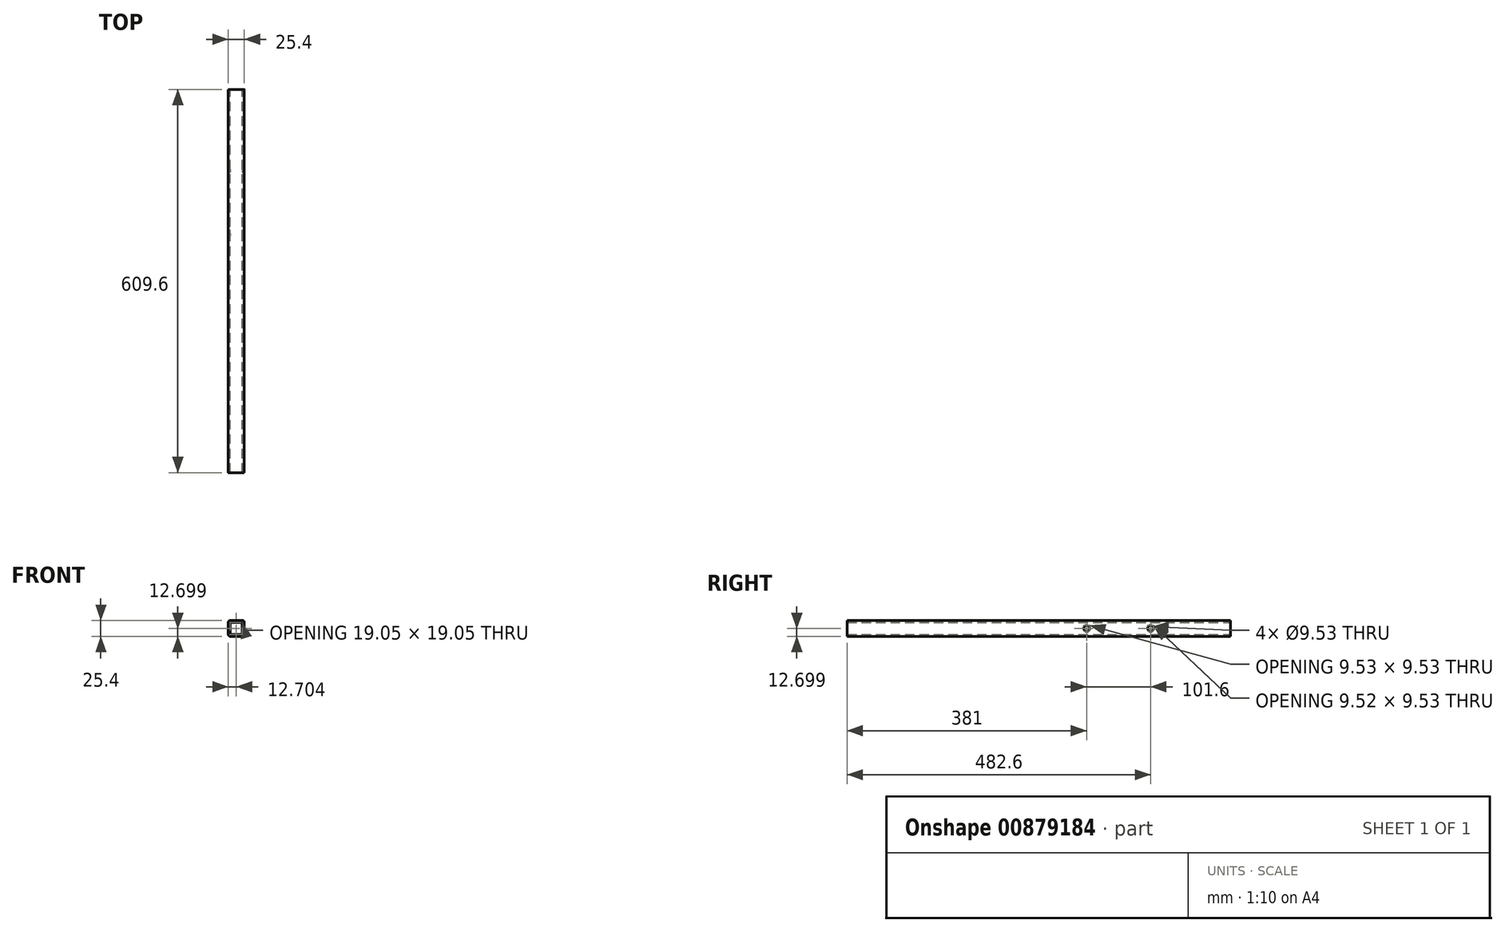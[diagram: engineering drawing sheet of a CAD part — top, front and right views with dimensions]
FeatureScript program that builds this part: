
annotation { "Feature Type Name" : "Feature", "Feature Type Description" : "" }
export const myFeature = defineFeature(function(context is Context, id is Id, definition is map)
    precondition{}
    {
        {
            var Q0;
            Q0=qCreatedBy(makeId("Front.planeOp"),FACE);
            var sketch = newSketch(context, id + "F0", { "sketchPlane" : qUnion([Q0])});
            skLineSegment(sketch, "E0.bottom", {"start": v(9.13, -11.87) * mm, "end": v(-9.92, -11.87) * mm});
            skLineSegment(sketch, "E0.top", {"start": v(9.13, 13.53) * mm, "end": v(-9.92, 13.53) * mm});
            skLineSegment(sketch, "E0.left", {"start": v(12.3, -8.7) * mm, "end": v(12.3, 10.35) * mm});
            skLineSegment(sketch, "E0.right", {"start": v(-13.1, -8.7) * mm, "end": v(-13.1, 10.35) * mm});
            skLineSegment(sketch, "E1.bottom", {"start": v(5.95, -8.7) * mm, "end": v(-6.75, -8.7) * mm});
            skLineSegment(sketch, "E1.top", {"start": v(5.95, 10.35) * mm, "end": v(-6.75, 10.35) * mm});
            skLineSegment(sketch, "E1.left", {"start": v(9.13, -5.52) * mm, "end": v(9.13, 7.18) * mm});
            skLineSegment(sketch, "E1.right", {"start": v(-9.92, -5.52) * mm, "end": v(-9.92, 7.18) * mm});
            skPoint(sketch, "E2.visualSharp", {"position": v(9.13, 10.35) * mm});
            skArc(sketch, "E2.filletArc", {"start": v(9.13, 7.18) * mm, "mid": v(8.2, 9.42) * mm, "end": v(5.95, 10.35) * mm});
            skPoint(sketch, "E3.visualSharp", {"position": v(-9.92, 10.35) * mm});
            skArc(sketch, "E3.filletArc", {"start": v(-6.75, 10.35) * mm, "mid": v(-9, 9.42) * mm, "end": v(-9.92, 7.18) * mm});
            skPoint(sketch, "E4.visualSharp", {"position": v(-9.92, -8.7) * mm});
            skArc(sketch, "E4.filletArc", {"start": v(-9.92, -5.52) * mm, "mid": v(-9, -7.77) * mm, "end": v(-6.75, -8.7) * mm});
            skPoint(sketch, "E5.visualSharp", {"position": v(9.13, -8.7) * mm});
            skArc(sketch, "E5.filletArc", {"start": v(5.95, -8.7) * mm, "mid": v(8.2, -7.77) * mm, "end": v(9.13, -5.52) * mm});
            skPoint(sketch, "E6.visualSharp", {"position": v(12.3, 13.53) * mm});
            skArc(sketch, "E6.filletArc", {"start": v(12.3, 10.35) * mm, "mid": v(11.37, 12.6) * mm, "end": v(9.13, 13.53) * mm});
            skPoint(sketch, "E7.visualSharp", {"position": v(-13.1, 13.53) * mm});
            skArc(sketch, "E7.filletArc", {"start": v(-9.92, 13.53) * mm, "mid": v(-12.17, 12.6) * mm, "end": v(-13.1, 10.35) * mm});
            skPoint(sketch, "E8.visualSharp", {"position": v(-13.1, -11.87) * mm});
            skArc(sketch, "E8.filletArc", {"start": v(-13.1, -8.7) * mm, "mid": v(-12.17, -10.94) * mm, "end": v(-9.92, -11.87) * mm});
            skPoint(sketch, "E9.visualSharp", {"position": v(12.3, -11.87) * mm});
            skArc(sketch, "E9.filletArc", {"start": v(9.13, -11.87) * mm, "mid": v(11.37, -10.94) * mm, "end": v(12.3, -8.7) * mm});
            skSolve(sketch);
        }
        {
            var Q0;
            Q0=qSketchRegion(id+"F0",true);
            extrude(context, id + "F1", {"entities" : qUnion([Q0]), "depth" : 609.6 * mm, "offsetDistance" : 25.4 * mm});
        }
        {
            var Q0;
            Q0=makeQuery(id+"F1.opExtrude","SWEPT_FACE",FACE,{"disambiguationData":[OSD([sQuery(id+"F0.wireOp",EDGE,"E0.left")])]});
            var sketch = newSketch(context, id + "F2", { "sketchPlane" : qUnion([Q0])});
            skCircle(sketch, "E10", {"center": v(-228.6, 0.83) * mm, "radius": 4.76 * mm});
            skCircle(sketch, "E11", {"center": v(-127, 0.83) * mm, "radius": 4.76 * mm});
            skSolve(sketch);
        }
        {
            var Q0;
            Q0=qSketchRegion(id+"F2",true);
            extrude(context, id + "F3", {"entities" : qUnion([Q0]), "operationType" : NewBodyOperationType.REMOVE, "oppositeDirection" : true, "depth" : 25.4 * mm, "offsetDistance" : 25.4 * mm});
        }
    });
